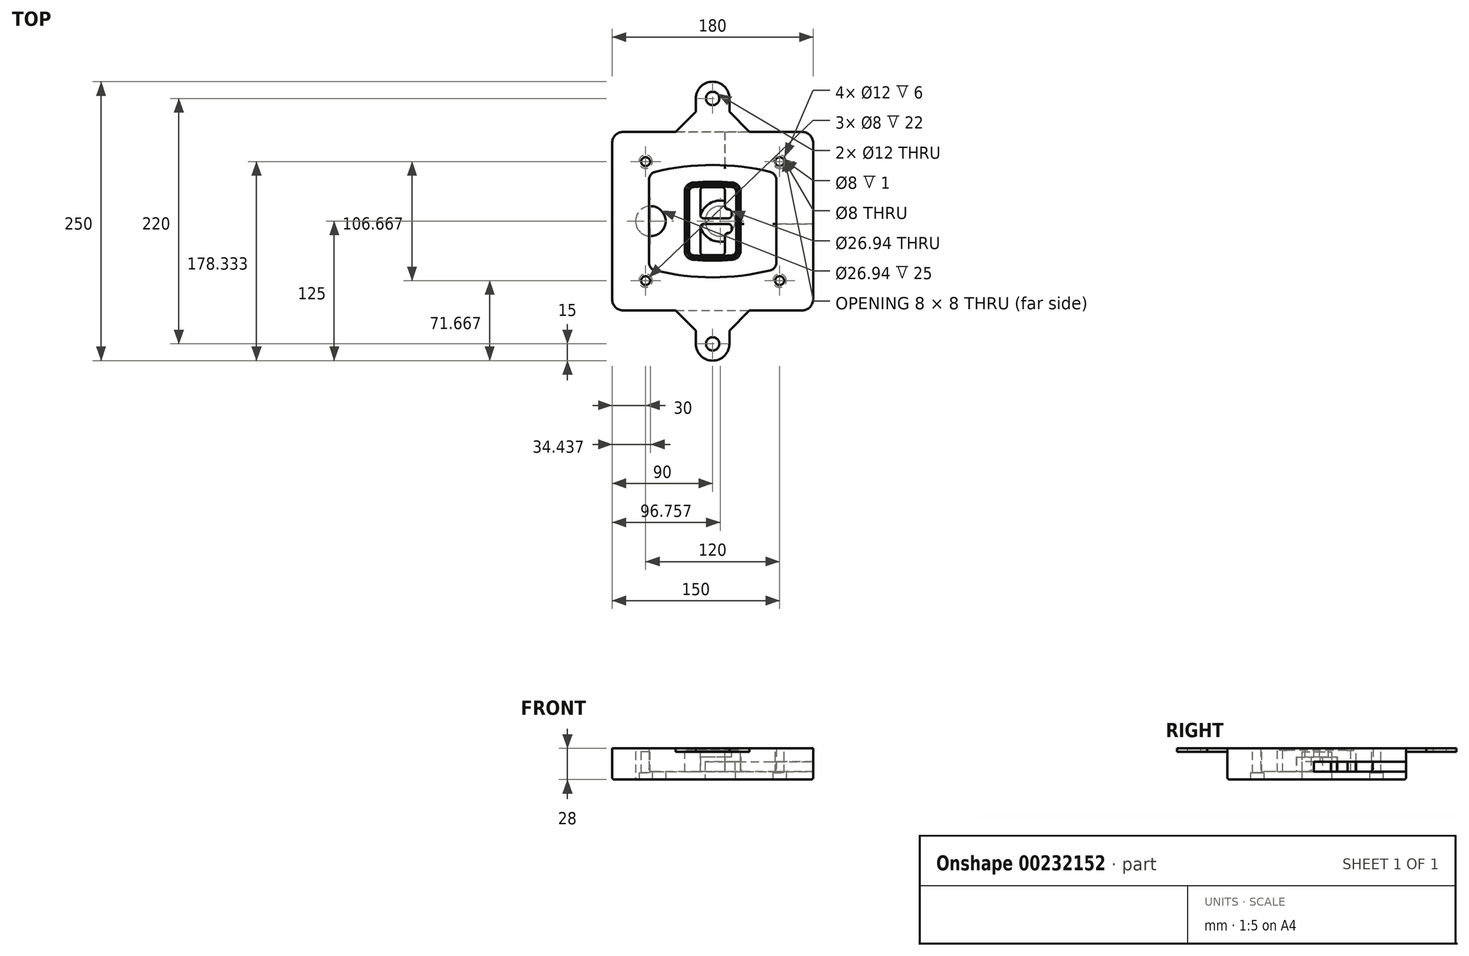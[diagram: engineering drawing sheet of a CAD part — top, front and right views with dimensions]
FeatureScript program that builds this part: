
annotation { "Feature Type Name" : "Feature", "Feature Type Description" : "" }
export const myFeature = defineFeature(function(context is Context, id is Id, definition is map)
    precondition{}
    {
        {
            var Q0;
            Q0=qCreatedBy(makeId("Top.planeOp"),FACE);
            var sketch = newSketch(context, id + "F0", { "sketchPlane" : qUnion([Q0])});
            skPoint(sketch, "E0.rect.middle", {"position": v(0, 0) * mm});
            skLineSegment(sketch, "E1.bottom", {"start": v(-80, -80) * mm, "end": v(80, -80) * mm});
            skLineSegment(sketch, "E1.top", {"start": v(-80, 80) * mm, "end": v(80, 80) * mm});
            skLineSegment(sketch, "E1.left", {"start": v(-90, -70) * mm, "end": v(-90, 70) * mm});
            skLineSegment(sketch, "E1.right", {"start": v(90, -70) * mm, "end": v(90, 70) * mm});
            skLineSegment(sketch, "E2", {"start": v(-90, 80) * mm, "end": v(90, -80) * mm, "construction": true});
            skLineSegment(sketch, "E3", {"start": v(90, 80) * mm, "end": v(-90, -80) * mm, "construction": true});
            skCircle(sketch, "E4", {"center": v(-60, 53.33) * mm, "radius": 4 * mm});
            skCircle(sketch, "E5", {"center": v(60, 53.33) * mm, "radius": 4 * mm});
            skCircle(sketch, "E6", {"center": v(60, -53.33) * mm, "radius": 4 * mm});
            skCircle(sketch, "E7", {"center": v(-60, -53.33) * mm, "radius": 4 * mm});
            skLineSegment(sketch, "E8", {"start": v(-60, 53.33) * mm, "end": v(60, 53.33) * mm, "construction": true});
            skLineSegment(sketch, "E9", {"start": v(60, 53.33) * mm, "end": v(60, -53.33) * mm, "construction": true});
            skLineSegment(sketch, "E10", {"start": v(60, -53.33) * mm, "end": v(-60, -53.33) * mm, "construction": true});
            skLineSegment(sketch, "E11", {"start": v(-60, -53.33) * mm, "end": v(-60, 53.33) * mm, "construction": true});
            skLineSegment(sketch, "E12", {"start": v(-60, 37.3) * mm, "end": v(-60, -37.3) * mm});
            skLineSegment(sketch, "E13", {"start": v(60, 37.3) * mm, "end": v(60, -37.3) * mm});
            skArc(sketch, "E14", {"start": v(52.38, 47.01) * mm, "mid": v(0, 53.33) * mm, "end": v(-52.38, 47.01) * mm});
            skArc(sketch, "E15", {"start": v(-52.38, -47.01) * mm, "mid": v(0, -53.33) * mm, "end": v(52.38, -47.01) * mm});
            skLineSegment(sketch, "E16", {"start": v(-60, 0) * mm, "end": v(60, 0) * mm, "construction": true});
            skPoint(sketch, "E17.visualSharp", {"position": v(-60, -45) * mm});
            skArc(sketch, "E17.filletArc", {"start": v(-60, -37.3) * mm, "mid": v(-57.87, -43.47) * mm, "end": v(-52.38, -47.01) * mm});
            skPoint(sketch, "E18.visualSharp", {"position": v(-60, 45) * mm});
            skArc(sketch, "E18.filletArc", {"start": v(-52.38, 47.01) * mm, "mid": v(-57.87, 43.47) * mm, "end": v(-60, 37.3) * mm});
            skPoint(sketch, "E19.visualSharp", {"position": v(60, 45) * mm});
            skArc(sketch, "E19.filletArc", {"start": v(60, 37.3) * mm, "mid": v(57.87, 43.47) * mm, "end": v(52.38, 47.01) * mm});
            skPoint(sketch, "E20.visualSharp", {"position": v(60, -45) * mm});
            skArc(sketch, "E20.filletArc", {"start": v(52.38, -47.01) * mm, "mid": v(57.87, -43.47) * mm, "end": v(60, -37.3) * mm});
            skPoint(sketch, "E21.visualSharp", {"position": v(-90, 80) * mm});
            skArc(sketch, "E21.filletArc", {"start": v(-80, 80) * mm, "mid": v(-87.07, 77.07) * mm, "end": v(-90, 70) * mm});
            skPoint(sketch, "E22.visualSharp", {"position": v(90, 80) * mm});
            skArc(sketch, "E22.filletArc", {"start": v(90, 70) * mm, "mid": v(87.07, 77.07) * mm, "end": v(80, 80) * mm});
            skPoint(sketch, "E23.visualSharp", {"position": v(90, -80) * mm});
            skArc(sketch, "E23.filletArc", {"start": v(80, -80) * mm, "mid": v(87.07, -77.07) * mm, "end": v(90, -70) * mm});
            skPoint(sketch, "E24.visualSharp", {"position": v(-90, -80) * mm});
            skArc(sketch, "E24.filletArc", {"start": v(-90, -70) * mm, "mid": v(-87.07, -77.07) * mm, "end": v(-80, -80) * mm});
            skArc(sketch, "E25.0", {"start": v(57, 37.3) * mm, "mid": v(55.5, 41.62) * mm, "end": v(51.67, 44.1) * mm});
            skLineSegment(sketch, "E25.1", {"start": v(57, 37.3) * mm, "end": v(57, -37.3) * mm});
            skArc(sketch, "E25.2", {"start": v(51.67, -44.1) * mm, "mid": v(55.5, -41.62) * mm, "end": v(57, -37.3) * mm});
            skArc(sketch, "E25.3", {"start": v(-51.67, -44.1) * mm, "mid": v(0, -50.33) * mm, "end": v(51.67, -44.1) * mm});
            skArc(sketch, "E25.4", {"start": v(-57, -37.3) * mm, "mid": v(-55.5, -41.62) * mm, "end": v(-51.67, -44.1) * mm});
            skArc(sketch, "E25.5", {"start": v(51.67, 44.1) * mm, "mid": v(0, 50.33) * mm, "end": v(-51.67, 44.1) * mm});
            skLineSegment(sketch, "E25.6", {"start": v(-57, 37.3) * mm, "end": v(-57, -37.3) * mm});
            skArc(sketch, "E25.7", {"start": v(-51.67, 44.1) * mm, "mid": v(-55.5, 41.62) * mm, "end": v(-57, 37.3) * mm});
            skArc(sketch, "E26.0", {"start": v(-53.33, 50.9) * mm, "mid": v(-61.01, 45.94) * mm, "end": v(-64, 37.3) * mm});
            skArc(sketch, "E26.1", {"start": v(53.33, 50.9) * mm, "mid": v(0, 57.33) * mm, "end": v(-53.33, 50.9) * mm});
            skArc(sketch, "E26.2", {"start": v(64, 37.3) * mm, "mid": v(61.01, 45.94) * mm, "end": v(53.33, 50.9) * mm});
            skLineSegment(sketch, "E26.3", {"start": v(64, 37.3) * mm, "end": v(64, -37.3) * mm});
            skArc(sketch, "E26.4", {"start": v(53.33, -50.9) * mm, "mid": v(61.01, -45.94) * mm, "end": v(64, -37.3) * mm});
            skLineSegment(sketch, "E26.5", {"start": v(-64, 37.3) * mm, "end": v(-64, -37.3) * mm});
            skArc(sketch, "E26.6", {"start": v(-53.33, -50.9) * mm, "mid": v(0, -57.33) * mm, "end": v(53.33, -50.9) * mm});
            skArc(sketch, "E26.7", {"start": v(-64, -37.3) * mm, "mid": v(-61.01, -45.94) * mm, "end": v(-53.33, -50.9) * mm});
            skSolve(sketch);
        }
        {
            var Q0;
            Q0=makeQuery(id+"F0.imprint","IMPRINT",FACE,{"disambiguationData":[TD([[makeQuery(id+"F0.imprint","IMPRINT",EDGE,{"derivedFrom":sQuery(id+"F0.wireOp",EDGE,"E1.bottom")}),1.0]])]});
            var Q1;
            Q1=makeQuery(id+"F0.imprint","IMPRINT",FACE,{"disambiguationData":[TD([[makeQuery(id+"F0.imprint","IMPRINT",EDGE,{"derivedFrom":sQuery(id+"F0.wireOp",EDGE,"E12")}),1.0]])]});
            var Q2;
            Q2=makeQuery(id+"F0.imprint","IMPRINT",FACE,{"disambiguationData":[TD([[makeQuery(id+"F0.imprint","IMPRINT",EDGE,{"derivedFrom":sQuery(id+"F0.wireOp",EDGE,"E25.0")}),1.0]])]});
            var Q3;
            Q3=makeQuery(id+"F0.imprint","IMPRINT",FACE,{"disambiguationData":[TD([[makeQuery(id+"F0.imprint","IMPRINT",EDGE,{"derivedFrom":sQuery(id+"F0.wireOp",EDGE,"E12")}),-1.0]])]});
            extrude(context, id + "F1", {"entities" : qUnion([Q0, Q1, Q2, Q3]), "oppositeDirection" : true, "depth" : 25 * mm});
        }
        {
            var Q0;
            Q0=makeQuery(id+"F0.imprint","IMPRINT",FACE,{"disambiguationData":[TD([[makeQuery(id+"F0.imprint","IMPRINT",EDGE,{"derivedFrom":sQuery(id+"F0.wireOp",EDGE,"E12")}),1.0]])]});
            extrude(context, id + "F2", {"entities" : qUnion([Q0]), "operationType" : NewBodyOperationType.ADD, "depth" : 3 * mm});
        }
        {
            var Q0;
            Q0=makeQuery(id+"F0.imprint","IMPRINT",FACE,{"disambiguationData":[TD([[makeQuery(id+"F0.imprint","IMPRINT",EDGE,{"derivedFrom":sQuery(id+"F0.wireOp",EDGE,"E25.0")}),1.0]])]});
            extrude(context, id + "F3", {"entities" : qUnion([Q0]), "operationType" : NewBodyOperationType.REMOVE, "oppositeDirection" : true, "depth" : 18 * mm});
        }
        {
            var Q0;
            Q0=makeQuery(id+"F2.opExtrude","CAP_FACE",FACE,{"disambiguationData":[OSD([sQuery(id+"F0.wireOp",EDGE,"E12"),sQuery(id+"F0.wireOp",EDGE,"E13"),sQuery(id+"F0.wireOp",EDGE,"E14"),sQuery(id+"F0.wireOp",EDGE,"E15"),sQuery(id+"F0.wireOp",EDGE,"E17.filletArc"),sQuery(id+"F0.wireOp",EDGE,"E18.filletArc"),sQuery(id+"F0.wireOp",EDGE,"E19.filletArc"),sQuery(id+"F0.wireOp",EDGE,"E20.filletArc"),sQuery(id+"F0.wireOp",EDGE,"E25.0"),sQuery(id+"F0.wireOp",EDGE,"E25.1"),sQuery(id+"F0.wireOp",EDGE,"E25.2"),sQuery(id+"F0.wireOp",EDGE,"E25.3"),sQuery(id+"F0.wireOp",EDGE,"E25.4"),sQuery(id+"F0.wireOp",EDGE,"E25.5"),sQuery(id+"F0.wireOp",EDGE,"E25.6"),sQuery(id+"F0.wireOp",EDGE,"E25.7")])],"isStart":false});
            var sketch = newSketch(context, id + "F4", { "sketchPlane" : qUnion([Q0])});
            skArc(sketch, "E27.0", {"start": v(-17.7, -34.56) * mm, "mid": v(0, -35.33) * mm, "end": v(17.7, -34.56) * mm});
            skArc(sketch, "E28.0", {"start": v(17.7, 34.56) * mm, "mid": v(0, 35.33) * mm, "end": v(-17.7, 34.56) * mm});
            skLineSegment(sketch, "E29", {"start": v(-25, 26.59) * mm, "end": v(-25, -26.59) * mm});
            skLineSegment(sketch, "E30", {"start": v(25, 26.59) * mm, "end": v(25, -26.59) * mm});
            skLineSegment(sketch, "E31", {"start": v(-25, 33.78) * mm, "end": v(25, 33.78) * mm, "construction": true});
            skLineSegment(sketch, "E32", {"start": v(-25, -33.78) * mm, "end": v(25, -33.78) * mm, "construction": true});
            skPoint(sketch, "E33.visualSharp", {"position": v(-25, 33.78) * mm});
            skArc(sketch, "E33.filletArc", {"start": v(-17.7, 34.56) * mm, "mid": v(-22.9, 32) * mm, "end": v(-25, 26.59) * mm});
            skPoint(sketch, "E34.visualSharp", {"position": v(25, 33.78) * mm});
            skArc(sketch, "E34.filletArc", {"start": v(25, 26.59) * mm, "mid": v(22.9, 32) * mm, "end": v(17.7, 34.56) * mm});
            skPoint(sketch, "E35.visualSharp", {"position": v(25, -33.78) * mm});
            skArc(sketch, "E35.filletArc", {"start": v(17.7, -34.56) * mm, "mid": v(22.9, -32) * mm, "end": v(25, -26.59) * mm});
            skPoint(sketch, "E36.visualSharp", {"position": v(-25, -33.78) * mm});
            skArc(sketch, "E36.filletArc", {"start": v(-25, -26.59) * mm, "mid": v(-22.9, -32) * mm, "end": v(-17.7, -34.56) * mm});
            skArc(sketch, "E37.0", {"start": v(51.67, 44.1) * mm, "mid": v(0, 50.33) * mm, "end": v(-51.67, 44.1) * mm});
            skArc(sketch, "E37.1", {"start": v(-51.67, 44.1) * mm, "mid": v(-55.5, 41.62) * mm, "end": v(-57, 37.3) * mm});
            skLineSegment(sketch, "E37.2", {"start": v(-57, 37.3) * mm, "end": v(-57, -37.3) * mm});
            skArc(sketch, "E37.3", {"start": v(-57, -37.3) * mm, "mid": v(-55.5, -41.62) * mm, "end": v(-51.67, -44.1) * mm});
            skArc(sketch, "E37.4", {"start": v(-51.67, -44.1) * mm, "mid": v(0, -50.33) * mm, "end": v(51.67, -44.1) * mm});
            skArc(sketch, "E37.5", {"start": v(51.67, -44.1) * mm, "mid": v(55.5, -41.62) * mm, "end": v(57, -37.3) * mm});
            skLineSegment(sketch, "E37.6", {"start": v(57, 37.3) * mm, "end": v(57, -37.3) * mm});
            skArc(sketch, "E37.7", {"start": v(57, 37.3) * mm, "mid": v(55.5, 41.62) * mm, "end": v(51.67, 44.1) * mm});
            skLineSegment(sketch, "E38.0", {"start": v(23, 26.59) * mm, "end": v(23, -26.59) * mm});
            skArc(sketch, "E38.1", {"start": v(17.53, -32.56) * mm, "mid": v(21.42, -30.64) * mm, "end": v(23, -26.59) * mm});
            skArc(sketch, "E38.2", {"start": v(-17.53, -32.56) * mm, "mid": v(0, -33.33) * mm, "end": v(17.53, -32.56) * mm});
            skArc(sketch, "E38.3", {"start": v(-23, -26.59) * mm, "mid": v(-21.42, -30.64) * mm, "end": v(-17.53, -32.56) * mm});
            skLineSegment(sketch, "E38.4", {"start": v(-23, 26.59) * mm, "end": v(-23, -26.59) * mm});
            skArc(sketch, "E38.5", {"start": v(23, 26.59) * mm, "mid": v(21.42, 30.64) * mm, "end": v(17.53, 32.56) * mm});
            skArc(sketch, "E38.6", {"start": v(-17.53, 32.56) * mm, "mid": v(-21.42, 30.64) * mm, "end": v(-23, 26.59) * mm});
            skArc(sketch, "E38.7", {"start": v(17.53, 32.56) * mm, "mid": v(0, 33.33) * mm, "end": v(-17.53, 32.56) * mm});
            skArc(sketch, "E39.0", {"start": v(21, 26.59) * mm, "mid": v(19.95, 29.29) * mm, "end": v(17.35, 30.57) * mm});
            skLineSegment(sketch, "E39.1", {"start": v(21, 26.59) * mm, "end": v(21, -26.59) * mm});
            skArc(sketch, "E39.2", {"start": v(17.35, -30.57) * mm, "mid": v(19.95, -29.29) * mm, "end": v(21, -26.59) * mm});
            skArc(sketch, "E39.3", {"start": v(-17.35, -30.57) * mm, "mid": v(0, -31.33) * mm, "end": v(17.35, -30.57) * mm});
            skArc(sketch, "E39.4", {"start": v(-21, -26.59) * mm, "mid": v(-19.95, -29.29) * mm, "end": v(-17.35, -30.57) * mm});
            skArc(sketch, "E39.5", {"start": v(17.35, 30.57) * mm, "mid": v(0, 31.33) * mm, "end": v(-17.35, 30.57) * mm});
            skLineSegment(sketch, "E39.6", {"start": v(-21, 26.59) * mm, "end": v(-21, -26.59) * mm});
            skArc(sketch, "E39.7", {"start": v(-17.35, 30.57) * mm, "mid": v(-19.95, 29.29) * mm, "end": v(-21, 26.59) * mm});
            skLineSegment(sketch, "E40", {"start": v(-25, 0) * mm, "end": v(25, 0) * mm, "construction": true});
            skLineSegment(sketch, "E41", {"start": v(-11, 5.5) * mm, "end": v(-11, 27.5) * mm});
            skLineSegment(sketch, "E42", {"start": v(-8, 30.5) * mm, "end": v(8, 30.5) * mm});
            skLineSegment(sketch, "E43", {"start": v(11, 27.5) * mm, "end": v(11, 13.5) * mm});
            skLineSegment(sketch, "E44", {"start": v(14, 10.5) * mm, "end": v(14, 10.5) * mm});
            skLineSegment(sketch, "E45", {"start": v(17, 7.5) * mm, "end": v(17, 5.5) * mm});
            skLineSegment(sketch, "E46", {"start": v(14, 2.5) * mm, "end": v(-8, 2.5) * mm});
            skPoint(sketch, "E47.visualSharp", {"position": v(-11, 30.5) * mm});
            skArc(sketch, "E47.filletArc", {"start": v(-8, 30.5) * mm, "mid": v(-10.12, 29.62) * mm, "end": v(-11, 27.5) * mm});
            skPoint(sketch, "E48.visualSharp", {"position": v(11, 30.5) * mm});
            skArc(sketch, "E48.filletArc", {"start": v(11, 27.5) * mm, "mid": v(10.12, 29.62) * mm, "end": v(8, 30.5) * mm});
            skPoint(sketch, "E49.visualSharp", {"position": v(11, 10.5) * mm});
            skArc(sketch, "E49.filletArc", {"start": v(11, 13.5) * mm, "mid": v(11.88, 11.38) * mm, "end": v(14, 10.5) * mm});
            skPoint(sketch, "E50.visualSharp", {"position": v(17, 10.5) * mm});
            skArc(sketch, "E50.filletArc", {"start": v(17, 7.5) * mm, "mid": v(16.12, 9.62) * mm, "end": v(14, 10.5) * mm});
            skPoint(sketch, "E51.visualSharp", {"position": v(17, 2.5) * mm});
            skArc(sketch, "E51.filletArc", {"start": v(14, 2.5) * mm, "mid": v(16.12, 3.38) * mm, "end": v(17, 5.5) * mm});
            skPoint(sketch, "E52.visualSharp", {"position": v(-11, 2.5) * mm});
            skArc(sketch, "E52.filletArc", {"start": v(-11, 5.5) * mm, "mid": v(-10.12, 3.38) * mm, "end": v(-8, 2.5) * mm});
            skLineSegment(sketch, "E53.0.MirrorCS", {"start": v(14, -2.5) * mm, "end": v(-8, -2.5) * mm});
            skArc(sketch, "E54.0.MirrorCS", {"start": v(-11, -5.5) * mm, "mid": v(-10.12, -3.38) * mm, "end": v(-8, -2.5) * mm});
            skLineSegment(sketch, "E55.0.MirrorCS", {"start": v(-11, -5.5) * mm, "end": v(-11, -27.5) * mm});
            skArc(sketch, "E56.0.MirrorCS", {"start": v(-8, -30.5) * mm, "mid": v(-10.12, -29.62) * mm, "end": v(-11, -27.5) * mm});
            skLineSegment(sketch, "E57.0.MirrorCS", {"start": v(-8, -30.5) * mm, "end": v(8, -30.5) * mm});
            skArc(sketch, "E58.0.MirrorCS", {"start": v(11, -27.5) * mm, "mid": v(10.12, -29.62) * mm, "end": v(8, -30.5) * mm});
            skLineSegment(sketch, "E59.0.MirrorCS", {"start": v(11, -27.5) * mm, "end": v(11, -13.5) * mm});
            skArc(sketch, "E60.0.MirrorCS", {"start": v(11, -13.5) * mm, "mid": v(11.88, -11.38) * mm, "end": v(14, -10.5) * mm});
            skArc(sketch, "E61.0.MirrorCS", {"start": v(17, -7.5) * mm, "mid": v(16.12, -9.62) * mm, "end": v(14, -10.5) * mm});
            skLineSegment(sketch, "E62.0.MirrorCS", {"start": v(17, -7.5) * mm, "end": v(17, -5.5) * mm});
            skArc(sketch, "E63.0.MirrorCS", {"start": v(14, -2.5) * mm, "mid": v(16.12, -3.38) * mm, "end": v(17, -5.5) * mm});
            skSolve(sketch);
        }
        {
            var Q0;
            Q0=makeQuery(id+"F4.imprint","IMPRINT",FACE,{"disambiguationData":[TD([[makeQuery(id+"F4.imprint","IMPRINT",EDGE,{"derivedFrom":sQuery(id+"F4.wireOp",EDGE,"E27.0")}),1.0]])]});
            var Q1;
            Q1=makeQuery(id+"F4.imprint","IMPRINT",FACE,{"disambiguationData":[TD([[makeQuery(id+"F4.imprint","IMPRINT",EDGE,{"derivedFrom":sQuery(id+"F4.wireOp",EDGE,"E38.0")}),-1.0]])]});
            var Q2;
            Q2=makeQuery(id+"F4.imprint","IMPRINT",FACE,{"disambiguationData":[TD([[makeQuery(id+"F4.imprint","IMPRINT",EDGE,{"derivedFrom":sQuery(id+"F4.wireOp",EDGE,"E39.0")}),1.0]])]});
            extrude(context, id + "F5", {"entities" : qUnion([Q0, Q1, Q2]), "operationType" : NewBodyOperationType.ADD, "endBound" : BoundingType.UP_TO_NEXT, "oppositeDirection" : true, "depth" : 25 * mm});
        }
        {
            var Q0;
            Q0=makeQuery(id+"F4.imprint","IMPRINT",FACE,{"disambiguationData":[TD([[makeQuery(id+"F4.imprint","IMPRINT",EDGE,{"derivedFrom":sQuery(id+"F4.wireOp",EDGE,"E38.0")}),-1.0]])]});
            extrude(context, id + "F6", {"entities" : qUnion([Q0]), "operationType" : NewBodyOperationType.REMOVE, "oppositeDirection" : true, "depth" : 2 * mm});
        }
        {
            var Q0;
            Q0=makeQuery(id+"F1.opExtrude","CAP_FACE",FACE,{"disambiguationData":[OSD([sQuery(id+"F0.wireOp",EDGE,"E1.bottom"),sQuery(id+"F0.wireOp",EDGE,"E1.top"),sQuery(id+"F0.wireOp",EDGE,"E1.left"),sQuery(id+"F0.wireOp",EDGE,"E1.right"),sQuery(id+"F0.wireOp",EDGE,"E4"),sQuery(id+"F0.wireOp",EDGE,"E5"),sQuery(id+"F0.wireOp",EDGE,"E6"),sQuery(id+"F0.wireOp",EDGE,"E7"),sQuery(id+"F0.wireOp",EDGE,"E21.filletArc"),sQuery(id+"F0.wireOp",EDGE,"E22.filletArc"),sQuery(id+"F0.wireOp",EDGE,"E23.filletArc"),sQuery(id+"F0.wireOp",EDGE,"E24.filletArc")])],"isStart":false});
            var sketch = newSketch(context, id + "F7", { "sketchPlane" : qUnion([Q0])});
            skCircle(sketch, "E64", {"center": v(6.76, 0) * mm, "radius": 13.47 * mm});
            skCircle(sketch, "E65", {"center": v(-55.56, 0) * mm, "radius": 13.47 * mm});
            skLineSegment(sketch, "E66", {"start": v(90, 0) * mm, "end": v(-90, 0) * mm});
            skCircle(sketch, "E67", {"center": v(6.76, 0) * mm, "radius": 18.47 * mm});
            skCircle(sketch, "E68", {"center": v(60, -53.33) * mm, "radius": 6 * mm});
            skCircle(sketch, "E69", {"center": v(-60, -53.33) * mm, "radius": 6 * mm});
            skCircle(sketch, "E70", {"center": v(-60, 53.33) * mm, "radius": 6 * mm});
            skCircle(sketch, "E71", {"center": v(60, 53.33) * mm, "radius": 6 * mm});
            skSolve(sketch);
        }
        {
            var Q0;
            {var subQ1=sQuery(id+"F7.wireOp",EDGE,"E66");var subQ4=sQuery(id+"F7.wireOp",EDGE,"E64");var subQ6=makeQuery(id+"F7.imprint","INTERSECT",VERTEX,{"disambiguationData":[OD(0.0)],"derivedFrom":[subQ4,subQ1]});Q0=makeQuery(id+"F7.imprint","IMPRINT",FACE,{"disambiguationData":[TD([[makeQuery(id+"F7.imprint","IMPRINT",EDGE,{"disambiguationData":[TD([[subQ6,-1.0]])],"derivedFrom":subQ4}),-1.0]])]});}
            var Q1;
            {var subQ0=sQuery(id+"F7.wireOp",EDGE,"E66");var subQ1=sQuery(id+"F7.wireOp",EDGE,"E64");var subQ3=makeQuery(id+"F7.imprint","INTERSECT",VERTEX,{"disambiguationData":[OD(0.0)],"derivedFrom":[subQ1,subQ0]});Q1=makeQuery(id+"F7.imprint","IMPRINT",FACE,{"disambiguationData":[TD([[makeQuery(id+"F7.imprint","IMPRINT",EDGE,{"disambiguationData":[TD([[subQ3,-1.0]])],"derivedFrom":subQ1}),1.0]])]});}
            var Q2;
            {var subQ0=sQuery(id+"F7.wireOp",EDGE,"E66");var subQ1=sQuery(id+"F7.wireOp",EDGE,"E64");var subQ3=makeQuery(id+"F7.imprint","INTERSECT",VERTEX,{"disambiguationData":[OD(0.0)],"derivedFrom":[subQ1,subQ0]});Q2=makeQuery(id+"F7.imprint","IMPRINT",FACE,{"disambiguationData":[TD([[makeQuery(id+"F7.imprint","IMPRINT",EDGE,{"disambiguationData":[TD([[subQ3,1.0]])],"derivedFrom":subQ1}),1.0]])]});}
            var Q3;
            {var subQ1=sQuery(id+"F7.wireOp",EDGE,"E66");var subQ4=sQuery(id+"F7.wireOp",EDGE,"E64");var subQ6=makeQuery(id+"F7.imprint","INTERSECT",VERTEX,{"disambiguationData":[OD(0.0)],"derivedFrom":[subQ4,subQ1]});Q3=makeQuery(id+"F7.imprint","IMPRINT",FACE,{"disambiguationData":[TD([[makeQuery(id+"F7.imprint","IMPRINT",EDGE,{"disambiguationData":[TD([[subQ6,1.0]])],"derivedFrom":subQ4}),-1.0]])]});}
            extrude(context, id + "F8", {"entities" : qUnion([Q0, Q1, Q2, Q3]), "operationType" : NewBodyOperationType.ADD, "oppositeDirection" : true, "depth" : 20 * mm});
        }
        {
            var Q0;
            {var subQ0=sQuery(id+"F7.wireOp",EDGE,"E66");var subQ1=sQuery(id+"F7.wireOp",EDGE,"E64");var subQ3=makeQuery(id+"F7.imprint","INTERSECT",VERTEX,{"disambiguationData":[OD(0.0)],"derivedFrom":[subQ1,subQ0]});Q0=makeQuery(id+"F7.imprint","IMPRINT",FACE,{"disambiguationData":[TD([[makeQuery(id+"F7.imprint","IMPRINT",EDGE,{"disambiguationData":[TD([[subQ3,-1.0]])],"derivedFrom":subQ1}),1.0]])]});}
            var Q1;
            {var subQ0=sQuery(id+"F7.wireOp",EDGE,"E66");var subQ1=sQuery(id+"F7.wireOp",EDGE,"E64");var subQ3=makeQuery(id+"F7.imprint","INTERSECT",VERTEX,{"disambiguationData":[OD(0.0)],"derivedFrom":[subQ1,subQ0]});Q1=makeQuery(id+"F7.imprint","IMPRINT",FACE,{"disambiguationData":[TD([[makeQuery(id+"F7.imprint","IMPRINT",EDGE,{"disambiguationData":[TD([[subQ3,1.0]])],"derivedFrom":subQ1}),1.0]])]});}
            extrude(context, id + "F9", {"entities" : qUnion([Q0, Q1]), "operationType" : NewBodyOperationType.REMOVE, "oppositeDirection" : true, "depth" : 16 * mm});
        }
        {
            var Q0;
            {var subQ0=sQuery(id+"F7.wireOp",EDGE,"E66");var subQ1=sQuery(id+"F7.wireOp",EDGE,"E65");var subQ3=makeQuery(id+"F7.imprint","INTERSECT",VERTEX,{"disambiguationData":[OD(0.0)],"derivedFrom":[subQ1,subQ0]});Q0=makeQuery(id+"F7.imprint","IMPRINT",FACE,{"disambiguationData":[TD([[makeQuery(id+"F7.imprint","IMPRINT",EDGE,{"disambiguationData":[TD([[subQ3,-1.0]])],"derivedFrom":subQ1}),1.0]])]});}
            var Q1;
            {var subQ0=sQuery(id+"F7.wireOp",EDGE,"E66");var subQ1=sQuery(id+"F7.wireOp",EDGE,"E65");var subQ3=makeQuery(id+"F7.imprint","INTERSECT",VERTEX,{"disambiguationData":[OD(0.0)],"derivedFrom":[subQ1,subQ0]});Q1=makeQuery(id+"F7.imprint","IMPRINT",FACE,{"disambiguationData":[TD([[makeQuery(id+"F7.imprint","IMPRINT",EDGE,{"disambiguationData":[TD([[subQ3,1.0]])],"derivedFrom":subQ1}),1.0]])]});}
            extrude(context, id + "F10", {"entities" : qUnion([Q0, Q1]), "operationType" : NewBodyOperationType.REMOVE, "oppositeDirection" : true, "depth" : 25 * mm});
        }
        {
            var Q0;
            Q0=makeQuery(id+"F7.imprint","IMPRINT",FACE,{"disambiguationData":[TD([[makeQuery(id+"F7.imprint","IMPRINT",EDGE,{"derivedFrom":sQuery(id+"F7.wireOp",EDGE,"E68")}),1.0]])]});
            var Q1;
            Q1=makeQuery(id+"F7.imprint","IMPRINT",FACE,{"disambiguationData":[TD([[makeQuery(id+"F7.imprint","IMPRINT",EDGE,{"derivedFrom":makeQuery(id+"F1.opExtrude","CAP_EDGE",EDGE,{"disambiguationData":[OSD([sQuery(id+"F0.wireOp",EDGE,"E5")])],"isStart":false})}),-1.0]])]});
            var Q2;
            Q2=makeQuery(id+"F7.imprint","IMPRINT",FACE,{"disambiguationData":[TD([[makeQuery(id+"F7.imprint","IMPRINT",EDGE,{"derivedFrom":sQuery(id+"F7.wireOp",EDGE,"E69")}),1.0]])]});
            var Q3;
            Q3=makeQuery(id+"F7.imprint","IMPRINT",FACE,{"disambiguationData":[TD([[makeQuery(id+"F7.imprint","IMPRINT",EDGE,{"derivedFrom":makeQuery(id+"F1.opExtrude","CAP_EDGE",EDGE,{"disambiguationData":[OSD([sQuery(id+"F0.wireOp",EDGE,"E4")])],"isStart":false})}),-1.0]])]});
            var Q4;
            Q4=makeQuery(id+"F7.imprint","IMPRINT",FACE,{"disambiguationData":[TD([[makeQuery(id+"F7.imprint","IMPRINT",EDGE,{"derivedFrom":sQuery(id+"F7.wireOp",EDGE,"E70")}),1.0]])]});
            var Q5;
            Q5=makeQuery(id+"F7.imprint","IMPRINT",FACE,{"disambiguationData":[TD([[makeQuery(id+"F7.imprint","IMPRINT",EDGE,{"derivedFrom":makeQuery(id+"F1.opExtrude","CAP_EDGE",EDGE,{"disambiguationData":[OSD([sQuery(id+"F0.wireOp",EDGE,"E7")])],"isStart":false})}),-1.0]])]});
            var Q6;
            Q6=makeQuery(id+"F7.imprint","IMPRINT",FACE,{"disambiguationData":[TD([[makeQuery(id+"F7.imprint","IMPRINT",EDGE,{"derivedFrom":sQuery(id+"F7.wireOp",EDGE,"E71")}),1.0]])]});
            var Q7;
            Q7=makeQuery(id+"F7.imprint","IMPRINT",FACE,{"disambiguationData":[TD([[makeQuery(id+"F7.imprint","IMPRINT",EDGE,{"derivedFrom":makeQuery(id+"F1.opExtrude","CAP_EDGE",EDGE,{"disambiguationData":[OSD([sQuery(id+"F0.wireOp",EDGE,"E6")])],"isStart":false})}),-1.0]])]});
            extrude(context, id + "F11", {"entities" : qUnion([Q0, Q1, Q2, Q3, Q4, Q5, Q6, Q7]), "operationType" : NewBodyOperationType.REMOVE, "oppositeDirection" : true, "depth" : 6 * mm});
        }
        {
            var Q0;
            Q0=makeQuery(id+"F9.boolean.opBoolean","COPY",FACE,{"derivedFrom":makeQuery(id+"F9.opExtrude","CAP_FACE",FACE,{"disambiguationData":[OSD([sQuery(id+"F7.wireOp",EDGE,"E64")])],"isStart":false})});
            var sketch = newSketch(context, id + "F12", { "sketchPlane" : qUnion([Q0])});
            skArc(sketch, "E72.0", {"start": v(11, -88.19) * mm, "mid": v(97.1, -83.6) * mm, "end": v(92.5, 2.5) * mm});
            skLineSegment(sketch, "E72.1", {"start": v(11, -17.97) * mm, "end": v(11, -17.97) * mm});
            skLineSegment(sketch, "E73", {"start": v(92.5, -105.13) * mm, "end": v(102.3, -105.13) * mm});
            skLineSegment(sketch, "E74.0", {"start": v(92.5, 2.5) * mm, "end": v(14, 2.5) * mm});
            skArc(sketch, "E74.1", {"start": v(14, 2.5) * mm, "mid": v(16.12, 3.38) * mm, "end": v(17, 5.5) * mm});
            skLineSegment(sketch, "E74.2", {"start": v(17, 7.5) * mm, "end": v(17, 5.5) * mm});
            skArc(sketch, "E74.3", {"start": v(17, 7.5) * mm, "mid": v(16.12, 9.62) * mm, "end": v(14, 10.5) * mm});
            skArc(sketch, "E74.4", {"start": v(11, 13.5) * mm, "mid": v(11.88, 11.38) * mm, "end": v(14, 10.5) * mm});
            skLineSegment(sketch, "E74.5", {"start": v(11, 13.5) * mm, "end": v(11, -88.19) * mm});
            skLineSegment(sketch, "E74.7", {"start": v(92.5, -2.5) * mm, "end": v(14, -2.5) * mm});
            skArc(sketch, "E74.8", {"start": v(14, -2.5) * mm, "mid": v(16.12, -3.38) * mm, "end": v(17, -5.5) * mm});
            skLineSegment(sketch, "E74.9", {"start": v(17, -7.5) * mm, "end": v(17, -5.5) * mm});
            skArc(sketch, "E74.10", {"start": v(17, -7.5) * mm, "mid": v(16.12, -9.62) * mm, "end": v(14, -10.5) * mm});
            skArc(sketch, "E74.11", {"start": v(11, -13.5) * mm, "mid": v(11.88, -11.38) * mm, "end": v(14, -10.5) * mm});
            skLineSegment(sketch, "E74.12", {"start": v(11, -17.97) * mm, "end": v(11, -13.5) * mm});
            skPoint(sketch, "E75.orphan", {"position": v(11, -27.5) * mm});
            skPoint(sketch, "E76.orphan", {"position": v(-8, -2.5) * mm});
            skPoint(sketch, "E77.orphan", {"position": v(-8, 2.5) * mm});
            skPoint(sketch, "E78.orphan", {"position": v(11, 27.5) * mm});
            skSolve(sketch);
        }
        {
            var Q0;
            {var subQ7=sQuery(id+"F12.wireOp",EDGE,"E72.0");var subQ14=sQuery(id+"F12.wireOp",EDGE,"E72.1");var subQ16=sQuery(id+"F12.wireOp",EDGE,"E74.1");var subQ18=sQuery(id+"F12.wireOp",EDGE,"E74.8");Q0=qUnion([makeQuery(id+"F12.imprint","IMPRINT",FACE,{"disambiguationData":[TD([[makeQuery(id+"F12.imprint","IMPRINT",EDGE,{"derivedFrom":subQ7}),1.0]])]}),makeQuery(id+"F12.imprint","IMPRINT",FACE,{"disambiguationData":[TD([[makeQuery(id+"F12.imprint","IMPRINT",EDGE,{"derivedFrom":subQ14}),1.0]])]}),makeQuery(id+"F12.imprint","IMPRINT",FACE,{"disambiguationData":[TD([[makeQuery(id+"F12.imprint","IMPRINT",EDGE,{"derivedFrom":subQ16}),1.0]])]}),makeQuery(id+"F12.imprint","IMPRINT",FACE,{"disambiguationData":[TD([[makeQuery(id+"F12.imprint","IMPRINT",EDGE,{"derivedFrom":subQ18}),-1.0]])]})]);}
            var Q1;
            Q1=makeQuery(id+"F5.boolean.opBoolean","SPLIT",FACE,{"disambiguationData":[TD([makeQuery(id+"F5.opExtrude","SWEPT_FACE",FACE,{"disambiguationData":[OSD([sQuery(id+"F4.wireOp",EDGE,"E41")])]})])],"derivedFrom":makeQuery(id+"F3.boolean.opBoolean","COPY",FACE,{"derivedFrom":makeQuery(id+"F3.opExtrude","CAP_FACE",FACE,{"disambiguationData":[OSD([sQuery(id+"F0.wireOp",EDGE,"E25.0"),sQuery(id+"F0.wireOp",EDGE,"E25.1"),sQuery(id+"F0.wireOp",EDGE,"E25.2"),sQuery(id+"F0.wireOp",EDGE,"E25.3"),sQuery(id+"F0.wireOp",EDGE,"E25.4"),sQuery(id+"F0.wireOp",EDGE,"E25.5"),sQuery(id+"F0.wireOp",EDGE,"E25.6"),sQuery(id+"F0.wireOp",EDGE,"E25.7")])],"isStart":false})})});
            extrude(context, id + "F13", {"entities" : qUnion([Q0]), "operationType" : NewBodyOperationType.REMOVE, "endBound" : BoundingType.UP_TO_SURFACE, "endBoundEntityFace" : qUnion([Q1]), "depth" : 25 * mm});
        }
        {
            var Q0;
            Q0=makeQuery(id+"F3.boolean.opBoolean","COPY",EDGE,{"derivedFrom":makeQuery(id+"F3.opExtrude","CAP_EDGE",EDGE,{"disambiguationData":[OSD([sQuery(id+"F0.wireOp",EDGE,"E25.6")])],"isStart":false})});
            var Q1;
            Q1=makeQuery(id+"F8.boolean.opBoolean","INTERSECT",EDGE,{"derivedFrom":[makeQuery(id+"F5.opExtrude","SWEPT_FACE",FACE,{"disambiguationData":[OSD([sQuery(id+"F4.wireOp",EDGE,"E30")])]}),makeQuery(id+"F8.opExtrude","CAP_FACE",FACE,{"disambiguationData":[OSD([sQuery(id+"F7.wireOp",EDGE,"E67")])],"isStart":false})]});
            var Q2;
            Q2=makeQuery(id+"F8.boolean.opBoolean","INTERSECT",EDGE,{"disambiguationData":[OD(1.0)],"derivedFrom":[makeQuery(id+"F5.opExtrude","SWEPT_FACE",FACE,{"disambiguationData":[OSD([sQuery(id+"F4.wireOp",EDGE,"E30")])]}),makeQuery(id+"F8.opExtrude","SWEPT_FACE",FACE,{"disambiguationData":[OSD([sQuery(id+"F7.wireOp",EDGE,"E67")])]})]});
            var Q3;
            {var subQ0=makeQuery(id+"F3.boolean.opBoolean","COPY",FACE,{"derivedFrom":makeQuery(id+"F3.opExtrude","CAP_FACE",FACE,{"disambiguationData":[OSD([sQuery(id+"F0.wireOp",EDGE,"E25.0"),sQuery(id+"F0.wireOp",EDGE,"E25.1"),sQuery(id+"F0.wireOp",EDGE,"E25.2"),sQuery(id+"F0.wireOp",EDGE,"E25.3"),sQuery(id+"F0.wireOp",EDGE,"E25.4"),sQuery(id+"F0.wireOp",EDGE,"E25.5"),sQuery(id+"F0.wireOp",EDGE,"E25.6"),sQuery(id+"F0.wireOp",EDGE,"E25.7")])],"isStart":false})});var subQ1=sQuery(id+"F4.wireOp",EDGE,"E30");Q3=makeQuery(id+"F8.boolean.opBoolean","SPLIT",EDGE,{"disambiguationData":[TD([makeQuery(id+"F5.opExtrude","SWEPT_FACE",FACE,{"disambiguationData":[OSD([sQuery(id+"F4.wireOp",EDGE,"E35.filletArc")])]})])],"derivedFrom":makeQuery(id+"F5.opExtrude","TWEAK_EDGE",EDGE,{"derivedFrom":[subQ0,makeQuery(id+"F4.imprint","IMPRINT",EDGE,{"derivedFrom":subQ1})]})});}
            var Q4;
            {var subQ0=sQuery(id+"F0.wireOp",EDGE,"E25.0");var subQ1=sQuery(id+"F0.wireOp",EDGE,"E25.1");var subQ2=sQuery(id+"F0.wireOp",EDGE,"E25.2");var subQ3=sQuery(id+"F0.wireOp",EDGE,"E25.3");var subQ4=sQuery(id+"F0.wireOp",EDGE,"E25.4");var subQ5=sQuery(id+"F0.wireOp",EDGE,"E25.5");var subQ6=sQuery(id+"F0.wireOp",EDGE,"E25.6");var subQ7=sQuery(id+"F0.wireOp",EDGE,"E25.7");Q4=makeQuery(id+"F8.boolean.opBoolean","INTERSECT",EDGE,{"derivedFrom":[makeQuery(id+"F5.boolean.opBoolean","SPLIT",FACE,{"disambiguationData":[TD([makeQuery(id+"F2.opExtrude","SWEPT_FACE",FACE,{"disambiguationData":[OSD([subQ0])]})])],"derivedFrom":makeQuery(id+"F3.boolean.opBoolean","COPY",FACE,{"derivedFrom":makeQuery(id+"F3.opExtrude","CAP_FACE",FACE,{"disambiguationData":[OSD([subQ0,subQ1,subQ2,subQ3,subQ4,subQ5,subQ6,subQ7])],"isStart":false})})}),makeQuery(id+"F8.opExtrude","SWEPT_FACE",FACE,{"disambiguationData":[OSD([sQuery(id+"F7.wireOp",EDGE,"E67")])]})]});}
            var Q5;
            Q5=makeQuery(id+"F8.boolean.opBoolean","INTERSECT",EDGE,{"disambiguationData":[OD(0.0)],"derivedFrom":[makeQuery(id+"F5.opExtrude","SWEPT_FACE",FACE,{"disambiguationData":[OSD([sQuery(id+"F4.wireOp",EDGE,"E30")])]}),makeQuery(id+"F8.opExtrude","SWEPT_FACE",FACE,{"disambiguationData":[OSD([sQuery(id+"F7.wireOp",EDGE,"E67")])]})]});
            fillet(context, id + "F14", {"entities" : qUnion([Q0, Q1, Q2, Q3, Q4, Q5]), "radius" : 3 * mm, "tangentPropagation" : true, "allowEdgeOverflow" : false});
        }
        {
            var Q0;
            Q0=makeQuery(id+"F1.opExtrude","CAP_EDGE",EDGE,{"disambiguationData":[OSD([sQuery(id+"F0.wireOp",EDGE,"E1.bottom")])],"isStart":false});
            fillet(context, id + "F15", {"entities" : qUnion([Q0]), "radius" : 2 * mm, "tangentPropagation" : true, "allowEdgeOverflow" : false});
        }
        {
            var Q0;
            {var subQ0=sQuery(id+"F0.wireOp",EDGE,"E22.filletArc");var subQ1=sQuery(id+"F0.wireOp",EDGE,"E7");var subQ2=sQuery(id+"F0.wireOp",EDGE,"E6");var subQ3=sQuery(id+"F0.wireOp",EDGE,"E5");var subQ4=sQuery(id+"F0.wireOp",EDGE,"E4");var subQ5=sQuery(id+"F0.wireOp",EDGE,"E1.bottom");var subQ6=sQuery(id+"F0.wireOp",EDGE,"E21.filletArc");var subQ7=sQuery(id+"F0.wireOp",EDGE,"E1.top");var subQ8=sQuery(id+"F0.wireOp",EDGE,"E1.left");var subQ9=sQuery(id+"F0.wireOp",EDGE,"E1.right");var subQ10=sQuery(id+"F0.wireOp",EDGE,"E23.filletArc");var subQ11=sQuery(id+"F0.wireOp",EDGE,"E24.filletArc");Q0=makeQuery(id+"F2.boolean.opBoolean","SPLIT",FACE,{"disambiguationData":[TD([makeQuery(id+"F1.opExtrude","SWEPT_FACE",FACE,{"disambiguationData":[OSD([subQ5])]})])],"derivedFrom":makeQuery(id+"F1.opExtrude","CAP_FACE",FACE,{"disambiguationData":[OSD([subQ5,subQ7,subQ8,subQ9,subQ4,subQ3,subQ2,subQ1,subQ6,subQ0,subQ10,subQ11])],"isStart":true})});}
            var sketch = newSketch(context, id + "F16", { "sketchPlane" : qUnion([Q0])});
            skLineSegment(sketch, "E79.0", {"start": v(-90, -70) * mm, "end": v(-90, 70) * mm});
            skLineSegment(sketch, "E79.1", {"start": v(-60, 37.3) * mm, "end": v(-60, -37.3) * mm});
            skArc(sketch, "E79.2", {"start": v(-52.38, -47.01) * mm, "mid": v(0, -53.33) * mm, "end": v(52.38, -47.01) * mm});
            skArc(sketch, "E79.3", {"start": v(-60, -37.3) * mm, "mid": v(-57.87, -43.47) * mm, "end": v(-52.38, -47.01) * mm});
            skArc(sketch, "E79.4", {"start": v(52.38, 47.01) * mm, "mid": v(0, 53.33) * mm, "end": v(-52.38, 47.01) * mm});
            skArc(sketch, "E79.5", {"start": v(-52.38, 47.01) * mm, "mid": v(-57.87, 43.47) * mm, "end": v(-60, 37.3) * mm});
            skLineSegment(sketch, "E79.6", {"start": v(90, -70) * mm, "end": v(90, 70) * mm});
            skLineSegment(sketch, "E79.7", {"start": v(-80, 80) * mm, "end": v(80, 80) * mm});
            skArc(sketch, "E79.8", {"start": v(-80, 80) * mm, "mid": v(-87.07, 77.07) * mm, "end": v(-90, 70) * mm});
            skArc(sketch, "E79.9", {"start": v(90, 70) * mm, "mid": v(87.07, 77.07) * mm, "end": v(80, 80) * mm});
            skArc(sketch, "E79.10", {"start": v(80, -80) * mm, "mid": v(87.07, -77.07) * mm, "end": v(90, -70) * mm});
            skLineSegment(sketch, "E79.11", {"start": v(-80, -80) * mm, "end": v(80, -80) * mm});
            skArc(sketch, "E79.12", {"start": v(-90, -70) * mm, "mid": v(-87.07, -77.07) * mm, "end": v(-80, -80) * mm});
            skCircle(sketch, "E79.13", {"center": v(-60, -53.33) * mm, "radius": 4 * mm});
            skCircle(sketch, "E79.14", {"center": v(60, -53.33) * mm, "radius": 4 * mm});
            skCircle(sketch, "E79.15", {"center": v(60, 53.33) * mm, "radius": 4 * mm});
            skCircle(sketch, "E79.16", {"center": v(-60, 53.33) * mm, "radius": 4 * mm});
            skLineSegment(sketch, "E79.17", {"start": v(60, 37.3) * mm, "end": v(60, -37.3) * mm});
            skArc(sketch, "E79.18", {"start": v(60, 37.3) * mm, "mid": v(57.87, 43.47) * mm, "end": v(52.38, 47.01) * mm});
            skArc(sketch, "E79.19", {"start": v(52.38, -47.01) * mm, "mid": v(57.87, -43.47) * mm, "end": v(60, -37.3) * mm});
            skLineSegment(sketch, "E80", {"start": v(0, 80) * mm, "end": v(0, 110) * mm});
            skLineSegment(sketch, "E81", {"start": v(32.95, 80) * mm, "end": v(14.95, 98) * mm});
            skLineSegment(sketch, "E82", {"start": v(14.95, 98) * mm, "end": v(14.95, 110) * mm});
            skLineSegment(sketch, "E83", {"start": v(-33.05, 80) * mm, "end": v(-15.05, 98) * mm});
            skLineSegment(sketch, "E84", {"start": v(-15.05, 98) * mm, "end": v(-15.05, 110) * mm});
            skCircle(sketch, "E85", {"center": v(0, 110) * mm, "radius": 6 * mm});
            skArc(sketch, "E86", {"start": v(14.95, 110) * mm, "mid": v(-0.05, 125) * mm, "end": v(-15.05, 110) * mm});
            skLineSegment(sketch, "E87", {"start": v(-90, 0) * mm, "end": v(90, 0) * mm, "construction": true});
            skLineSegment(sketch, "E88.MirrorCS", {"start": v(-15.05, -98) * mm, "end": v(-15.05, -110) * mm});
            skLineSegment(sketch, "E89.MirrorCS", {"start": v(-33.05, -80) * mm, "end": v(-15.05, -98) * mm});
            skLineSegment(sketch, "E90.MirrorCS", {"start": v(14.95, -98) * mm, "end": v(14.95, -110) * mm});
            skArc(sketch, "E91.MirrorCS", {"start": v(14.95, -110) * mm, "mid": v(-0.05, -125) * mm, "end": v(-15.05, -110) * mm});
            skCircle(sketch, "E92.MirrorC", {"center": v(0, -110) * mm, "radius": 6 * mm});
            skLineSegment(sketch, "E93.MirrorCS", {"start": v(0, -80) * mm, "end": v(0, -110) * mm});
            skLineSegment(sketch, "E94.MirrorCS", {"start": v(32.95, -80) * mm, "end": v(14.95, -98) * mm});
            skSolve(sketch);
        }
        {
            var Q0;
            Q0 = qSketchRegion(id + "F16", true);
            var Q1;
            Q1=makeQuery(id+"F2.opExtrude","CAP_FACE",FACE,{"disambiguationData":[OSD([sQuery(id+"F0.wireOp",EDGE,"E12"),sQuery(id+"F0.wireOp",EDGE,"E13"),sQuery(id+"F0.wireOp",EDGE,"E14"),sQuery(id+"F0.wireOp",EDGE,"E15"),sQuery(id+"F0.wireOp",EDGE,"E17.filletArc"),sQuery(id+"F0.wireOp",EDGE,"E18.filletArc"),sQuery(id+"F0.wireOp",EDGE,"E19.filletArc"),sQuery(id+"F0.wireOp",EDGE,"E20.filletArc"),sQuery(id+"F0.wireOp",EDGE,"E25.0"),sQuery(id+"F0.wireOp",EDGE,"E25.1"),sQuery(id+"F0.wireOp",EDGE,"E25.2"),sQuery(id+"F0.wireOp",EDGE,"E25.3"),sQuery(id+"F0.wireOp",EDGE,"E25.4"),sQuery(id+"F0.wireOp",EDGE,"E25.5"),sQuery(id+"F0.wireOp",EDGE,"E25.6"),sQuery(id+"F0.wireOp",EDGE,"E25.7")])],"isStart":false});
            extrude(context, id + "F17", {"entities" : qUnion([Q0]), "operationType" : NewBodyOperationType.ADD, "endBound" : BoundingType.UP_TO_SURFACE, "endBoundEntityFace" : qUnion([Q1]), "depth" : 25 * mm});
        }
    });
